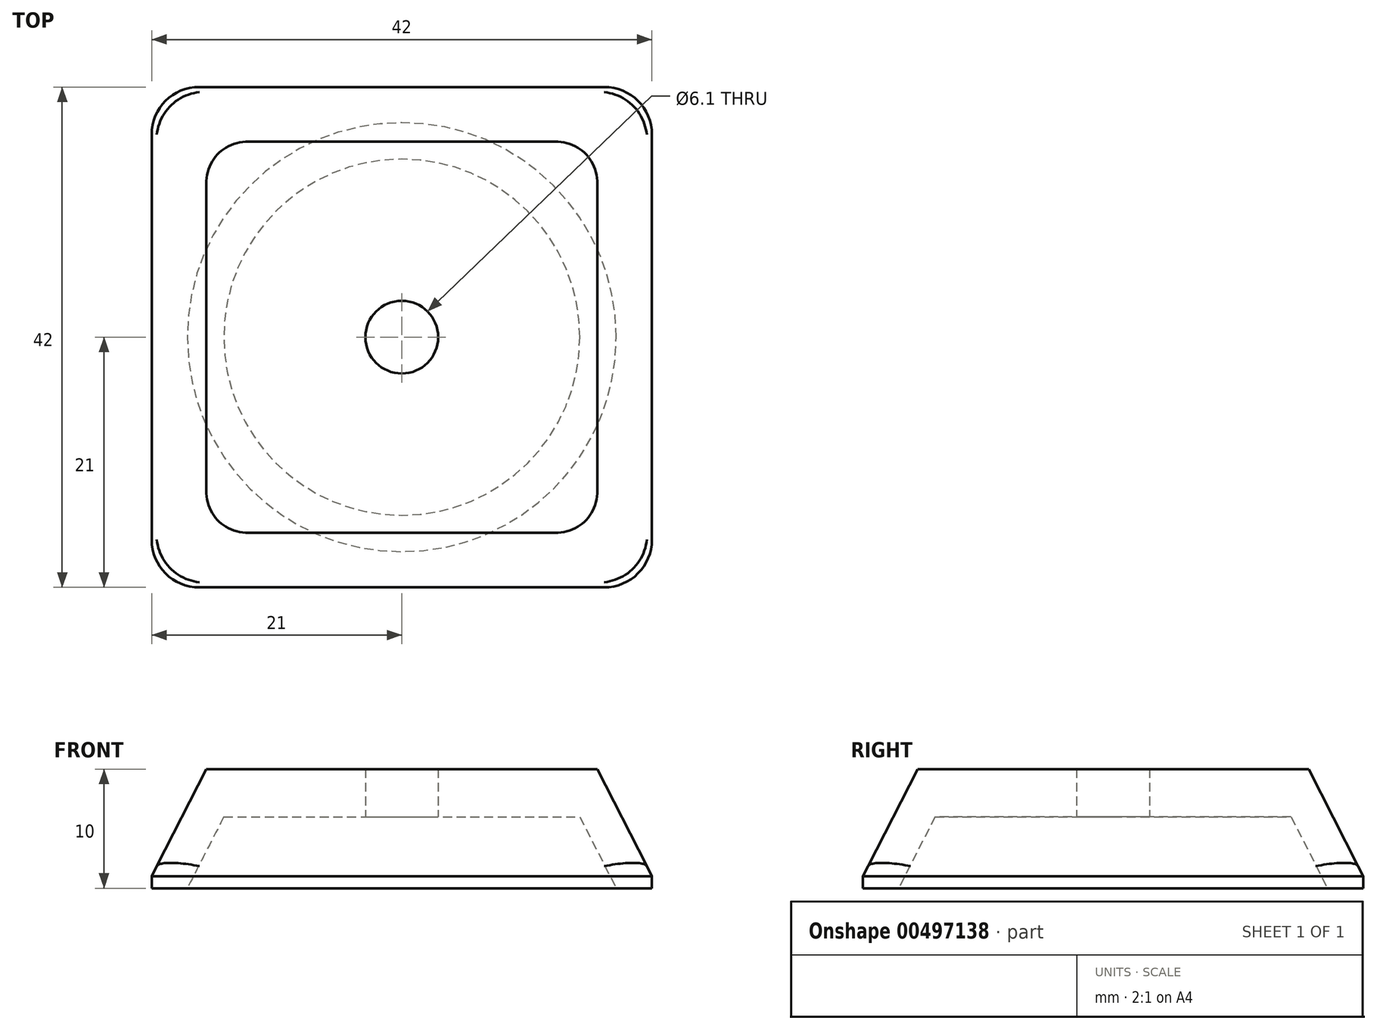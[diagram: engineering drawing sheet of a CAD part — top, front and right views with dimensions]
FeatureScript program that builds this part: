
annotation { "Feature Type Name" : "Feature", "Feature Type Description" : "" }
export const myFeature = defineFeature(function(context is Context, id is Id, definition is map)
    precondition{}
    {
        {
            var Q0;
            Q0=qCreatedBy(makeId("Top.planeOp"),FACE);
            var sketch = newSketch(context, id + "F0", { "sketchPlane" : qUnion([Q0])});
            skLineSegment(sketch, "E0.bottom", {"start": v(17, -21) * mm, "end": v(-17, -21) * mm});
            skLineSegment(sketch, "E0.top", {"start": v(17, 21) * mm, "end": v(-17, 21) * mm});
            skLineSegment(sketch, "E0.left", {"start": v(21, -17) * mm, "end": v(21, 17) * mm});
            skLineSegment(sketch, "E0.right", {"start": v(-21, -17) * mm, "end": v(-21, 17) * mm});
            skPoint(sketch, "E0.middle", {"position": v(0, 0) * mm});
            skPoint(sketch, "E1.visualSharp", {"position": v(-21, 21) * mm});
            skArc(sketch, "E1.filletArc", {"start": v(-17, 21) * mm, "mid": v(-19.83, 19.83) * mm, "end": v(-21, 17) * mm});
            skPoint(sketch, "E2.visualSharp", {"position": v(21, 21) * mm});
            skArc(sketch, "E2.filletArc", {"start": v(21, 17) * mm, "mid": v(19.83, 19.83) * mm, "end": v(17, 21) * mm});
            skPoint(sketch, "E3.visualSharp", {"position": v(21, -21) * mm});
            skArc(sketch, "E3.filletArc", {"start": v(17, -21) * mm, "mid": v(19.83, -19.83) * mm, "end": v(21, -17) * mm});
            skPoint(sketch, "E4.visualSharp", {"position": v(-21, -21) * mm});
            skArc(sketch, "E4.filletArc", {"start": v(-21, -17) * mm, "mid": v(-19.83, -19.83) * mm, "end": v(-17, -21) * mm});
            skSolve(sketch);
        }
        {
            var Q0;
            Q0=makeQuery(id+"F0.imprint","IMPRINT",FACE,{"disambiguationData":[TD([[makeQuery(id+"F0.imprint","IMPRINT",EDGE,{"derivedFrom":sQuery(id+"F0.wireOp",EDGE,"E0.bottom")}),-1.0]])]});
            extrude(context, id + "F1", {"entities" : qUnion([Q0]), "depth" : 1 * mm, "offsetDistance" : 25 * mm});
        }
        {
            var Q0;
            Q0=makeQuery(id+"F1.opExtrude","CAP_FACE",FACE,{"disambiguationData":[OSD([sQuery(id+"F0.wireOp",EDGE,"E0.bottom"),sQuery(id+"F0.wireOp",EDGE,"E0.top"),sQuery(id+"F0.wireOp",EDGE,"E0.left"),sQuery(id+"F0.wireOp",EDGE,"E0.right"),sQuery(id+"F0.wireOp",EDGE,"E1.filletArc"),sQuery(id+"F0.wireOp",EDGE,"E2.filletArc"),sQuery(id+"F0.wireOp",EDGE,"E3.filletArc"),sQuery(id+"F0.wireOp",EDGE,"E4.filletArc")])],"isStart":false});
            extrude(context, id + "F2", {"entities" : qUnion([Q0]), "operationType" : NewBodyOperationType.ADD, "depth" : 9 * mm, "offsetDistance" : 25 * mm, "hasDraft" : true, "draftAngle" : 27 * degree, "draftPullDirection" : true});
        }
        {
            var Q0;
            {var subQ0=sQuery(id+"F0.wireOp",EDGE,"E4.filletArc");Q0=makeQuery(id+"F2.*.draft.opDraft","MERGE",EDGE,{"derivedFrom":[makeQuery(id+"F2.opExtrude","SWEPT_EDGE",EDGE,{"disambiguationData":[OSD([sQuery(id+"F0.wireOp",EDGE,"E0.bottom"),subQ0])]}),makeQuery(id+"F2.opExtrude","SWEPT_EDGE",EDGE,{"disambiguationData":[OSD([sQuery(id+"F0.wireOp",EDGE,"E0.right"),subQ0])]})]});}
            var Q1;
            {var subQ0=sQuery(id+"F0.wireOp",EDGE,"E3.filletArc");Q1=makeQuery(id+"F2.*.draft.opDraft","MERGE",EDGE,{"derivedFrom":[makeQuery(id+"F2.opExtrude","SWEPT_EDGE",EDGE,{"disambiguationData":[OSD([sQuery(id+"F0.wireOp",EDGE,"E0.bottom"),subQ0])]}),makeQuery(id+"F2.opExtrude","SWEPT_EDGE",EDGE,{"disambiguationData":[OSD([sQuery(id+"F0.wireOp",EDGE,"E0.left"),subQ0])]})]});}
            var Q2;
            {var subQ0=sQuery(id+"F0.wireOp",EDGE,"E2.filletArc");Q2=makeQuery(id+"F2.*.draft.opDraft","MERGE",EDGE,{"derivedFrom":[makeQuery(id+"F2.opExtrude","SWEPT_EDGE",EDGE,{"disambiguationData":[OSD([sQuery(id+"F0.wireOp",EDGE,"E0.top"),subQ0])]}),makeQuery(id+"F2.opExtrude","SWEPT_EDGE",EDGE,{"disambiguationData":[OSD([sQuery(id+"F0.wireOp",EDGE,"E0.left"),subQ0])]})]});}
            var Q3;
            {var subQ0=sQuery(id+"F0.wireOp",EDGE,"E1.filletArc");Q3=makeQuery(id+"F2.*.draft.opDraft","MERGE",EDGE,{"derivedFrom":[makeQuery(id+"F2.opExtrude","SWEPT_EDGE",EDGE,{"disambiguationData":[OSD([sQuery(id+"F0.wireOp",EDGE,"E0.top"),subQ0])]}),makeQuery(id+"F2.opExtrude","SWEPT_EDGE",EDGE,{"disambiguationData":[OSD([sQuery(id+"F0.wireOp",EDGE,"E0.right"),subQ0])]})]});}
            fillet(context, id + "F3", {"entities" : qUnion([Q0, Q1, Q2, Q3]), "radius" : 4 * mm, "tangentPropagation" : true, "allowEdgeOverflow" : false});
        }
        {
            var Q0;
            Q0=makeQuery(id+"F1.opExtrude","CAP_FACE",FACE,{"disambiguationData":[OSD([sQuery(id+"F0.wireOp",EDGE,"E0.bottom"),sQuery(id+"F0.wireOp",EDGE,"E0.top"),sQuery(id+"F0.wireOp",EDGE,"E0.left"),sQuery(id+"F0.wireOp",EDGE,"E0.right"),sQuery(id+"F0.wireOp",EDGE,"E1.filletArc"),sQuery(id+"F0.wireOp",EDGE,"E2.filletArc"),sQuery(id+"F0.wireOp",EDGE,"E3.filletArc"),sQuery(id+"F0.wireOp",EDGE,"E4.filletArc")])],"isStart":true});
            var sketch = newSketch(context, id + "F4", { "sketchPlane" : qUnion([Q0])});
            skCircle(sketch, "E5", {"center": v(0, 0) * mm, "radius": 18 * mm});
            skSolve(sketch);
        }
        {
            var Q0;
            Q0=makeQuery(id+"F4.imprint","IMPRINT",FACE,{"disambiguationData":[TD([[makeQuery(id+"F4.imprint","IMPRINT",EDGE,{"derivedFrom":sQuery(id+"F4.wireOp",EDGE,"E5")}),1.0]])]});
            extrude(context, id + "F5", {"entities" : qUnion([Q0]), "operationType" : NewBodyOperationType.REMOVE, "oppositeDirection" : true, "depth" : 6 * mm, "offsetDistance" : 25 * mm, "hasDraft" : true, "draftAngle" : 27 * degree, "draftPullDirection" : true});
        }
        {
            var Q0;
            Q0=makeQuery(id+"F5.boolean.opBoolean","COPY",FACE,{"derivedFrom":makeQuery(id+"F5.opExtrude","CAP_FACE",FACE,{"disambiguationData":[OSD([sQuery(id+"F4.wireOp",EDGE,"E5")])],"isStart":false})});
            var sketch = newSketch(context, id + "F6", { "sketchPlane" : qUnion([Q0])});
            skCircle(sketch, "E6", {"center": v(0, 0) * mm, "radius": 3.05 * mm});
            skSolve(sketch);
        }
        {
            var Q0;
            Q0=makeQuery(id+"F6.imprint","IMPRINT",FACE,{"disambiguationData":[TD([[makeQuery(id+"F6.imprint","IMPRINT",EDGE,{"derivedFrom":sQuery(id+"F6.wireOp",EDGE,"E6")}),1.0]])]});
            var Q1;
            Q1=sQuery(id+"F6.wireOp",EDGE,"E6");
            extrude(context, id + "F7", {"entities" : qUnion([Q0]), "operationType" : NewBodyOperationType.REMOVE, "surfaceEntities" : qUnion([Q1]), "endBound" : BoundingType.THROUGH_ALL, "oppositeDirection" : true, "depth" : 25 * mm, "offsetDistance" : 25 * mm});
        }
    });
